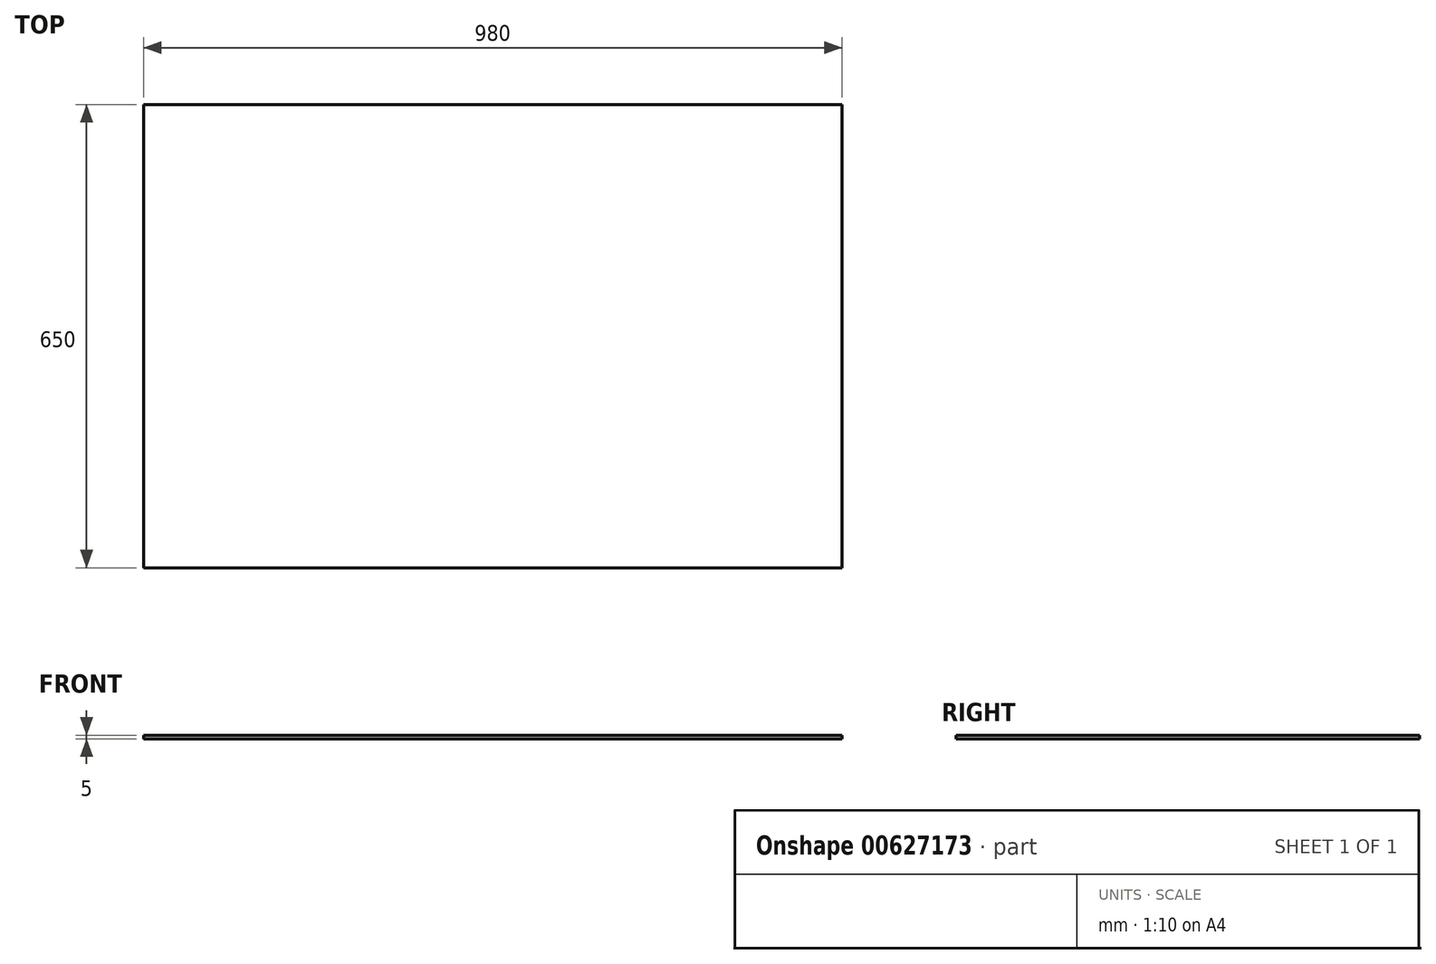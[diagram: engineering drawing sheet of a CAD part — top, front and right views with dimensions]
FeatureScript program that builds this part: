
annotation { "Feature Type Name" : "Feature", "Feature Type Description" : "" }
export const myFeature = defineFeature(function(context is Context, id is Id, definition is map)
    precondition{}
    {
        {
            var Q0;
            Q0=qCreatedBy(makeId("Top.planeOp"),FACE);
            var sketch = newSketch(context, id + "F0", { "sketchPlane" : qUnion([Q0])});
            skLineSegment(sketch, "E0.bottom", {"start": v(490, -325) * mm, "end": v(-490, -325) * mm});
            skLineSegment(sketch, "E0.top", {"start": v(490, 325) * mm, "end": v(-490, 325) * mm});
            skLineSegment(sketch, "E0.left", {"start": v(490, -325) * mm, "end": v(490, 325) * mm});
            skLineSegment(sketch, "E0.right", {"start": v(-490, -325) * mm, "end": v(-490, 325) * mm});
            skPoint(sketch, "E0.middle", {"position": v(0, 0) * mm});
            skSolve(sketch);
        }
        {
            var Q0;
            Q0 = qSketchRegion(id + "F0", true);
            extrude(context, id + "F1", {"entities" : qUnion([Q0]), "depth" : 5 * mm, "offsetDistance" : 25 * mm});
        }
    });
